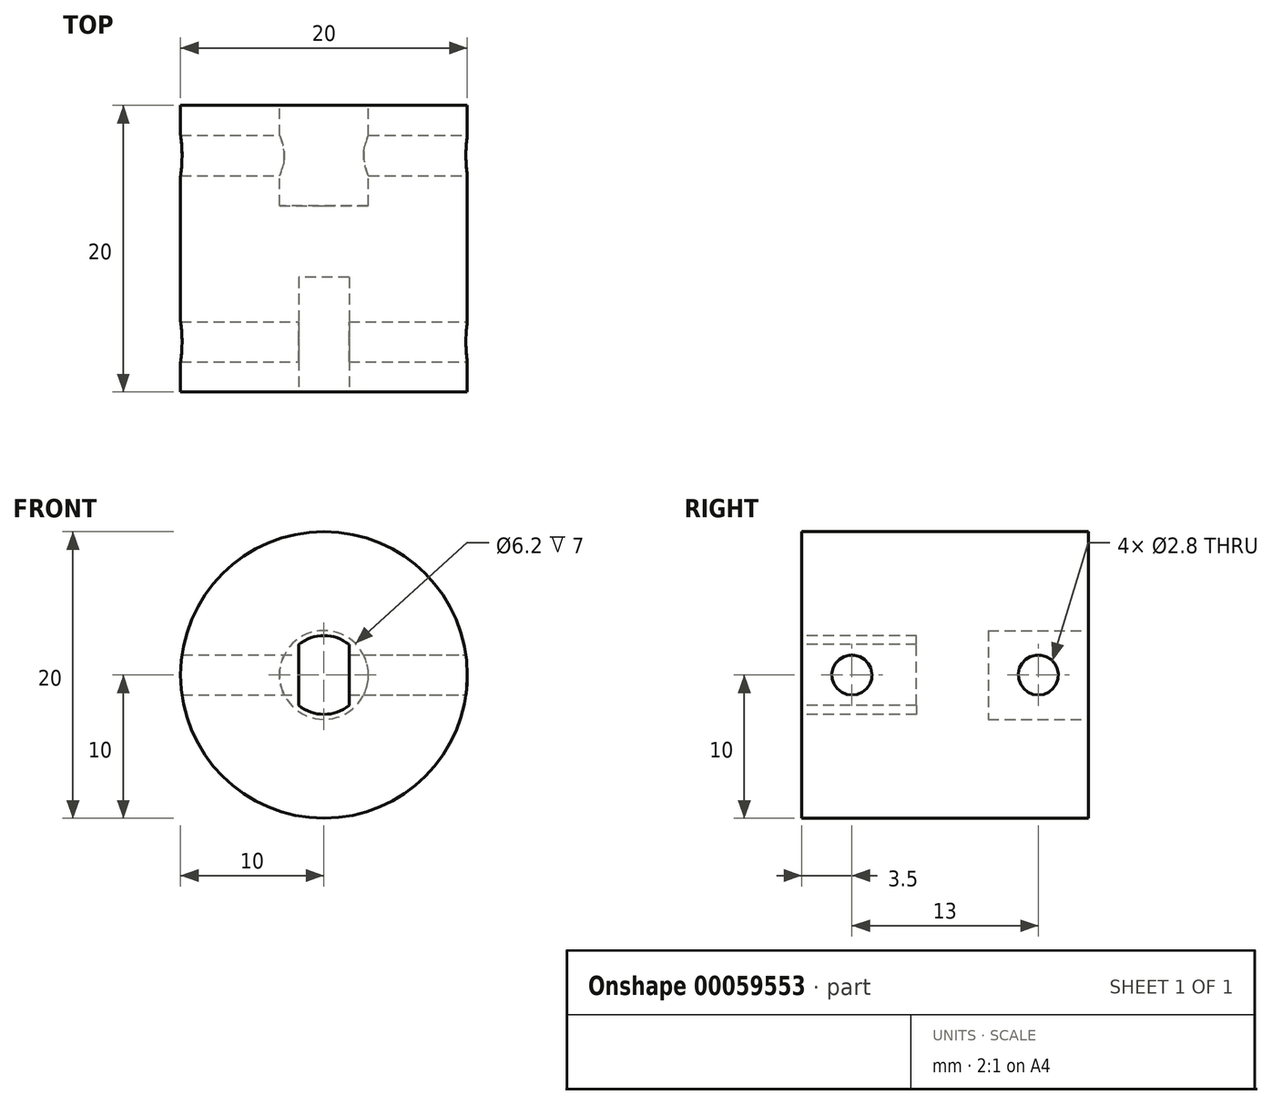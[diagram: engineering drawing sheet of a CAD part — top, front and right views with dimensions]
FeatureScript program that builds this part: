
annotation { "Feature Type Name" : "Feature", "Feature Type Description" : "" }
export const myFeature = defineFeature(function(context is Context, id is Id, definition is map)
    precondition{}
    {
        {
            var Q0;
            Q0=qCreatedBy(makeId("Front.planeOp"),FACE);
            var sketch = newSketch(context, id + "F0", { "sketchPlane" : qUnion([Q0])});
            skCircle(sketch, "E0", {"center": v(0, 0) * mm, "radius": 10 * mm});
            skSolve(sketch);
        }
        {
            var Q0;
            Q0 = qSketchRegion(id + "F0", true);
            extrude(context, id + "F1", {"entities" : qUnion([Q0]), "depth" : 20 * mm});
        }
        {
            var Q0;
            Q0=makeQuery(id+"F1.opExtrude","CAP_FACE",FACE,{"disambiguationData":[OSD([sQuery(id+"F0.wireOp",EDGE,"E0")])],"isStart":false});
            var sketch = newSketch(context, id + "F2", { "sketchPlane" : qUnion([Q0])});
            skArc(sketch, "E1", {"start": v(1.75, 2.12) * mm, "mid": v(0, 2.75) * mm, "end": v(-1.75, 2.12) * mm});
            skLineSegment(sketch, "E2.left", {"start": v(-1.75, -2.12) * mm, "end": v(-1.75, 2.12) * mm});
            skLineSegment(sketch, "E2.right", {"start": v(1.75, -2.12) * mm, "end": v(1.75, 2.12) * mm});
            skArc(sketch, "E3.trimOffspring", {"start": v(-1.75, -2.12) * mm, "mid": v(0, -2.75) * mm, "end": v(1.75, -2.12) * mm});
            skSolve(sketch);
        }
        {
            var Q0;
            Q0 = qSketchRegion(id + "F2", true);
            extrude(context, id + "F3", {"entities" : qUnion([Q0]), "operationType" : NewBodyOperationType.REMOVE, "oppositeDirection" : true, "depth" : 8 * mm});
        }
        {
            var Q0;
            Q0=makeQuery(id+"F1.opExtrude","CAP_FACE",FACE,{"disambiguationData":[OSD([sQuery(id+"F0.wireOp",EDGE,"E0")])],"isStart":true});
            var sketch = newSketch(context, id + "F4", { "sketchPlane" : qUnion([Q0])});
            skCircle(sketch, "E4", {"center": v(0, 0) * mm, "radius": 3.1 * mm});
            skSolve(sketch);
        }
        {
            var Q0;
            Q0 = qSketchRegion(id + "F4", true);
            extrude(context, id + "F5", {"entities" : qUnion([Q0]), "operationType" : NewBodyOperationType.REMOVE, "oppositeDirection" : true, "depth" : 7 * mm});
        }
        {
            var Q0;
            Q0=qCreatedBy(makeId("Right.planeOp"),FACE);
            var sketch = newSketch(context, id + "F6", { "sketchPlane" : qUnion([Q0])});
            skCircle(sketch, "E5", {"center": v(-3.5, 0) * mm, "radius": 1.4 * mm});
            skLineSegment(sketch, "E6", {"start": v(0, 0) * mm, "end": v(-20, 0) * mm, "construction": true});
            skLineSegment(sketch, "E7", {"start": v(-10, 0) * mm, "end": v(-10, 9.98) * mm, "construction": true});
            skCircle(sketch, "E8.MirrorC", {"center": v(-16.5, 0) * mm, "radius": 1.4 * mm});
            skSolve(sketch);
        }
        {
            var Q0;
            Q0 = qSketchRegion(id + "F6", true);
            extrude(context, id + "F7", {"entities" : qUnion([Q0]), "operationType" : NewBodyOperationType.REMOVE, "endBound" : BoundingType.SYMMETRIC, "oppositeDirection" : true, "depth" : 25 * mm});
        }
    });
